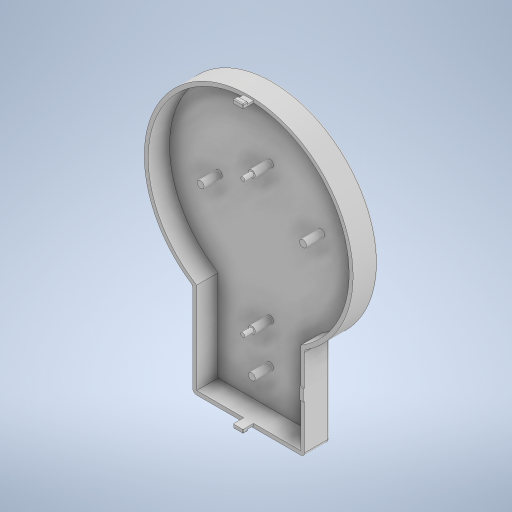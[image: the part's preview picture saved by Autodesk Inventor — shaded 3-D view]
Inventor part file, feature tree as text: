
AUTODESK INVENTOR PART (.ipt)
format: ipt  version: 2024 (Build 280153000, 153)  size: 476,160 bytes
history: native  units: mm
features: extrude x11, sketch x11, fillet x5
ambient origin geometry x8: Origin, YZ Plane, XZ Plane, XY Plane, X Axis, Y Axis, Z Axis, Center Point
bodies: Body1 (feature_tree)
feature tree (27):
  extrude  "Extrusion2"  Depth=102.0mm
  sketch  "Esquisse2"
  extrude  "Extrusion5"  Depth=26.4mm
  sketch  "Esquisse4"
  sketch  "Esquisse5"
  extrude  "Extrusion6"  Depth=90.0mm
  extrude  "Extrusion7"  Depth=26.4mm
  extrude  "Extrusion8"  Depth=2.0mm TaperAngle=0.0deg
  extrude  "Extrusion10"  Depth=3.5mm
  fillet  "Congé2"  Radius=39.1mm
  fillet  "Congé3"  Radius=26.4mm
  extrude  "Extrusion11"  Depth=3.5mm
  extrude  "Extrusion12"  Depth=107.68mm
  extrude  "Extrusion13"  Depth=26.4mm
  fillet  "Congé4"  Radius=9.2mm
  fillet  "Congé6"  Radius=2.0mm
  extrude  "Extrusion14"  Depth=2.0mm
  extrude  "Extrusion17"  Depth=4.6mm TaperAngle=0.0deg
  fillet  "Congé7"  Radius=4.6mm
  sketch  "Esquisse1"
  sketch  "Esquisse6"
  sketch  "Esquisse7"
  sketch  "Esquisse8"
  sketch  "Esquisse9"
  sketch  "Esquisse10"
  sketch  "Esquisse11"
  sketch  "Esquisse17"
